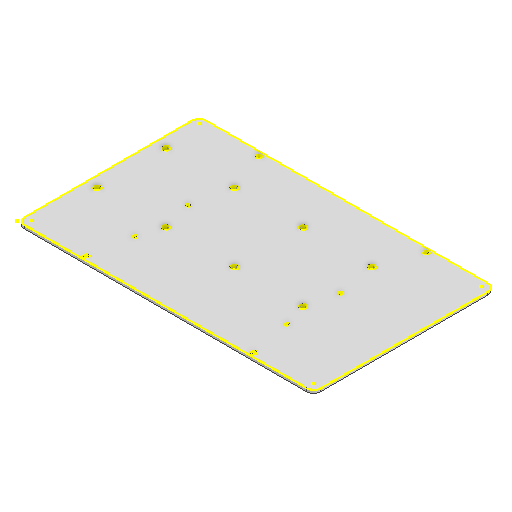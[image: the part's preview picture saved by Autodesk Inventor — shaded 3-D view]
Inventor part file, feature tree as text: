
AUTODESK INVENTOR PART (.ipt)
format: ipt  version: 2023 (Build 270158000, 158)  size: 162,816 bytes
history: native  units: mm
features: sketch x3, extrude x2, fillet x1, projected_geometry x1
ambient origin geometry x8: Origin, YZ Plane, XZ Plane, XY Plane, X Axis, Y Axis, Z Axis, Center Point
bodies: Solid1 (feature_tree)
feature tree (7):
  extrude  "Extrusion1"  Depth=132.08mm
  extrude  "Extrusion2"  Depth=20.0mm
  fillet  "Fillet1"  Radius=46.99mm
  sketch  "Sketch3"  dims[d12=3.072mm d13=3.072mm d14=4.4mm d15=50.0mm d16=8.0mm d17=20.0mm d19=50.0mm d20=40.0mm d22=50.0mm d25=2.54mm d26=0.0mm d27=1.0mm d28=0.0mm d29=5.0mm d30=2.5mm d31=20.0mm d33=111.0mm d34=20.0mm d36=39.0mm d39=60.0mm d40=52.45mm]
  sketch  "Sketch1"  dims[d0=215.9mm d1=132.08mm]
  sketch  "Sketch2"  dims[d2=3.3mm d3=20.0mm d5=121.92mm d6=20.0mm d8=125.936mm d11=46.99mm]
  projected_geometry  "Projected Loop1"
